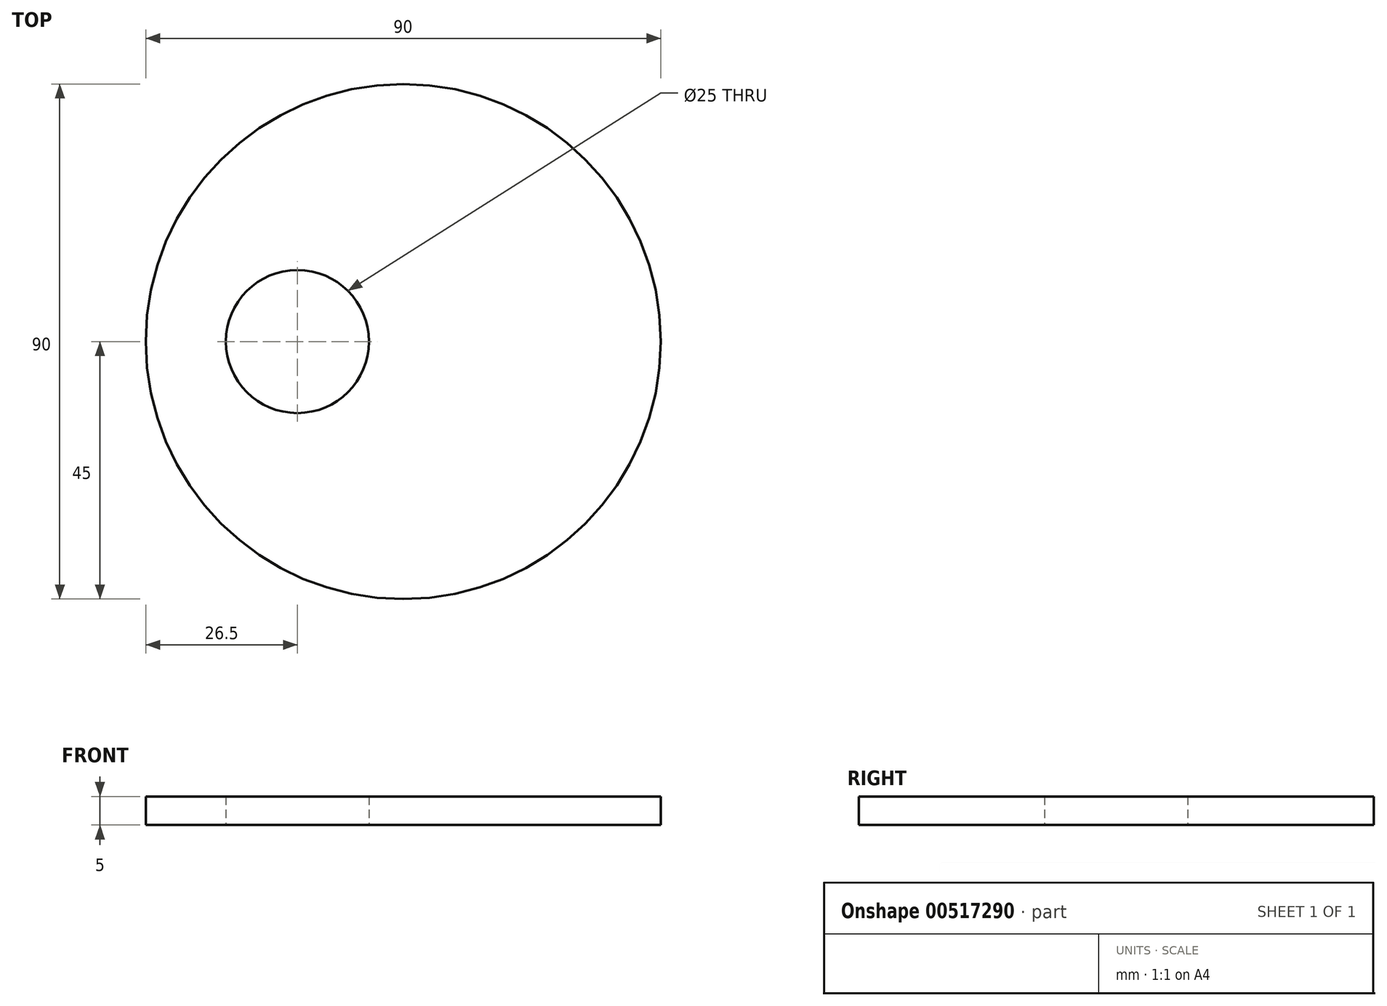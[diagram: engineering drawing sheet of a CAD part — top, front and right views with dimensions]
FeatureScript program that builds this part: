
annotation { "Feature Type Name" : "Feature", "Feature Type Description" : "" }
export const myFeature = defineFeature(function(context is Context, id is Id, definition is map)
    precondition{}
    {
        {
            var Q0;
            Q0=qCreatedBy(makeId("Top.planeOp"),FACE);
            var sketch = newSketch(context, id + "F0", { "sketchPlane" : qUnion([Q0])});
            skCircle(sketch, "E0", {"center": v(0, 0) * mm, "radius": 45 * mm});
            skCircle(sketch, "E1", {"center": v(-18.5, 0) * mm, "radius": 12.5 * mm});
            skSolve(sketch);
        }
        {
            var Q0;
            Q0 = qSketchRegion(id + "F0", true);
            extrude(context, id + "F1", {"entities" : qUnion([Q0]), "depth" : 5 * mm, "offsetDistance" : 25 * mm});
        }
    });
